# Revit family: Platek_Blend Bollard
name_source: partatom
category: Apparecchi per illuminazione
revit_build: Autodesk Revit 2017 (Build: 20160225_1515(x64)
units: mm (PartAtom-declared; Revit-internal decimal feet)

## family parameters
Basato su piano di lavoro = No
Condiviso = No
Punto di calcolo locali = No
Quota connettore circolare = Usa diametro
Sempre verticale = Sì
Sorgente d'illuminazione = No
Taglio con vuoti quando caricato = No
Tipo di parte = Normale

## types (2) — shared parameters
Aluminium = PLK_Aluminium
Body = PLK_06_Grey
CRI = >80
Carico apparente = 0 VA
Colour Temperature = 3000 K
Commenti sul tipo = Pedestrian areas, Urban zones, Paths, Roads
Descrizione = Outdoor Lighting, Floor/Ground Illumination
Diffuse Type = PMMA
Energy Efficiency Rating = A/A+/A++
Frequency = 50/60 Hz
IK Rating = IK10
IP Rating = IP65
Insulation Class = 1
LED Protection = Surge protection included
Light Source = PLK_Light Source
Modello = BLEND BOLLARD
Mounting Type = Ground
Nota chiave = Other Led colors available on request
PLATEK FInishes = Painted Aluminium, Avalaible in Grey/White/Bronze/Black/Anthracite
Power Supply Unit = Included
Product Documentation Link = http://www.platek.eu
Product Page URL = http://www.platek.eu
Produttore = PLATEK SRL
Supply Voltage = 230 V
Supply Voltage Max = 240 V
Supply Voltage Min = 220 V
URL = www.platek.eu

## per-type parameters (varying)
| type | Angolo di inclinazione | Codice assieme | Dimmable | Height 300_900 | Immagine tipo | Lampada | Luminaire Luminous Flux | Luminaire Luminous Intensity | Luminaire Wattage | Manufacturer Comment | PLATEK Article Code | PLK | Product Dimension |
| 1640519_10W_LED_3000K_H300mm | 0.00° | 1640519.06(Grey); 1640519.08(Anthracite); 1640519.01(Black); 1640519.02(White); 1640519.07(Corten); 1640519.09(Bronze) | On Request | Sì | blend_paletto_300_2.jpg | LED | 720 lm | 266 cd | 10 W | Weight 3,5 Kg | 1640519 | PLK_Photometrics_1640519 | L160mm x L160mm x H300mm |
| 1640619_19,5W_LED_3000K_900mm | 90.00° | 1640619.06(Grey); 1640619.08(Anthracite); 1640619.01(Black); 1640619.02(White); 1640619.07(Corten); 1640619.09(Bronze) | On request | No | blend_paletto_900_1.jpg | 2 LED | 1300 lm | 1450 cd | 20 W | Weight 8 Kg | 1640619 | PLK_Photometrics_1640619 | L160mm x L160mm x H900mm |

## geometry (parser evidence)
native form markers: Blend x2
no freeform markers — native parametric forms only
